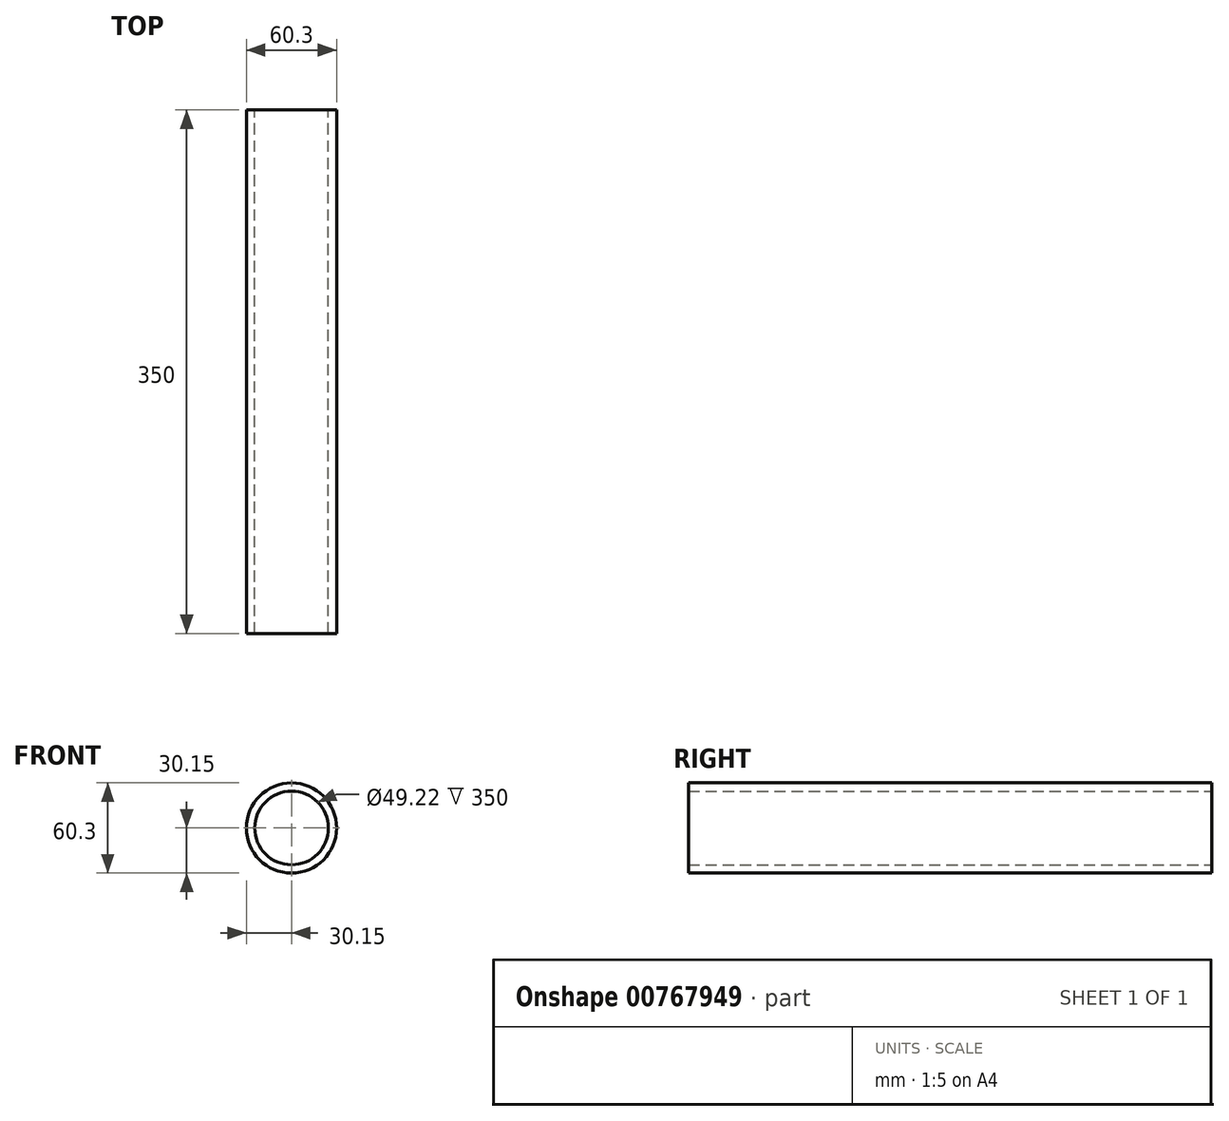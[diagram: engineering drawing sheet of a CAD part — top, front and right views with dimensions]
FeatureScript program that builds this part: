
annotation { "Feature Type Name" : "Feature", "Feature Type Description" : "" }
export const myFeature = defineFeature(function(context is Context, id is Id, definition is map)
    precondition{}
    {
        {
            var Q0;
            Q0=qCreatedBy(makeId("Front.planeOp"),FACE);
            var sketch = newSketch(context, id + "F0", { "sketchPlane" : qUnion([Q0])});
            skCircle(sketch, "E0", {"center": v(0, 0) * mm, "radius": 30.15 * mm});
            skCircle(sketch, "E1", {"center": v(0, 0) * mm, "radius": 24.6 * mm});
            skSolve(sketch);
        }
        {
            var Q0;
            Q0 = qSketchRegion(id + "F0", true);
            extrude(context, id + "F1", {"entities" : qUnion([Q0]), "depth" : 350 * mm, "offsetDistance" : 25 * mm});
        }
    });
